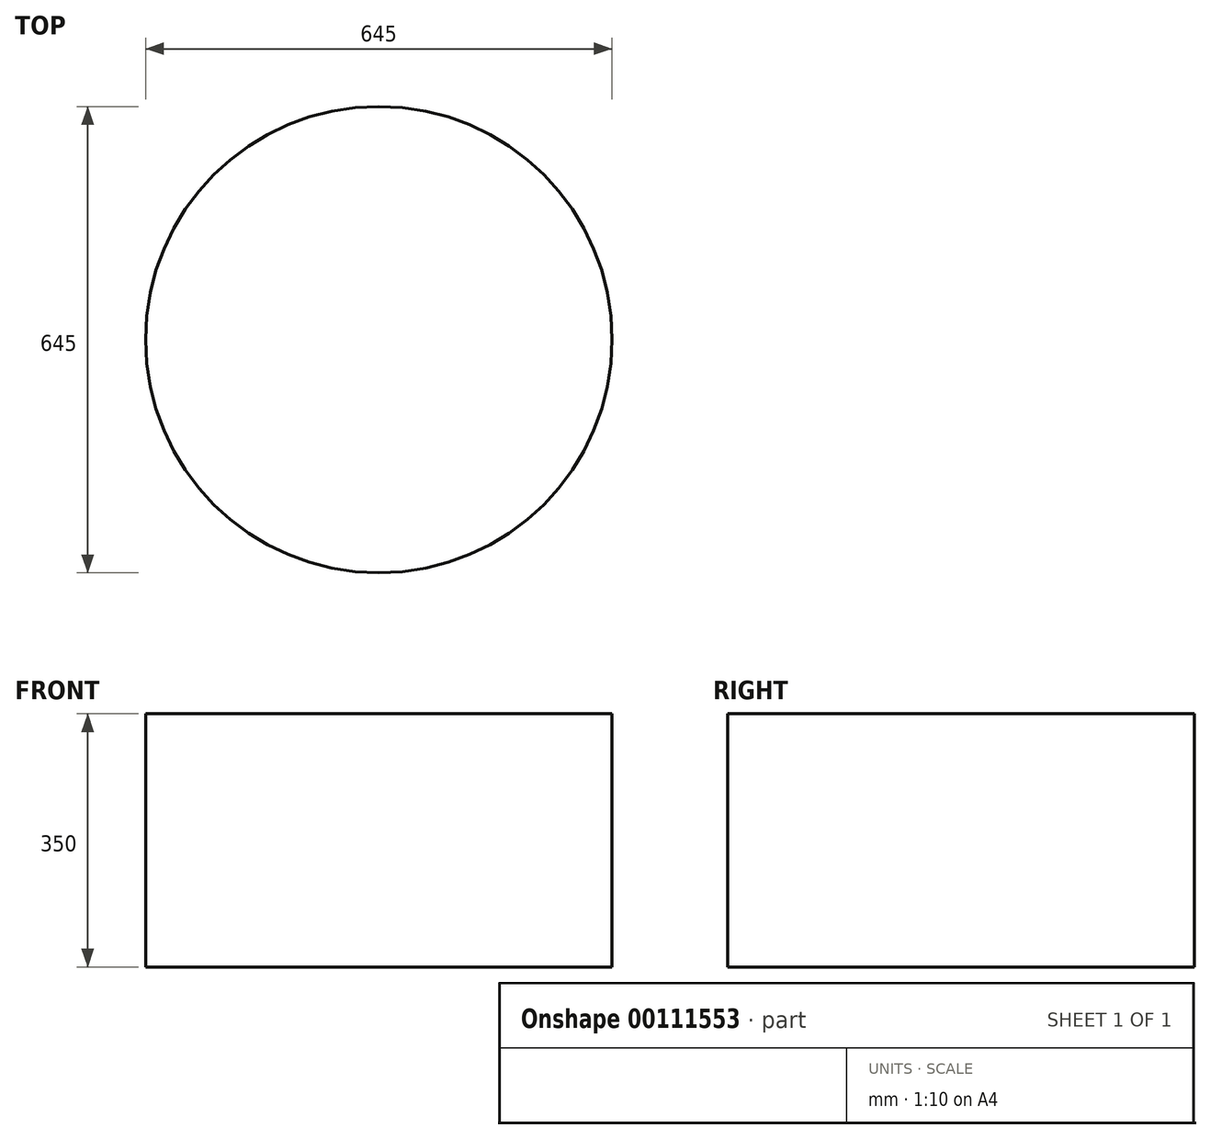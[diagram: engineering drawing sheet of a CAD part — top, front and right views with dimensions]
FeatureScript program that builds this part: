
annotation { "Feature Type Name" : "Feature", "Feature Type Description" : "" }
export const myFeature = defineFeature(function(context is Context, id is Id, definition is map)
    precondition{}
    {
        {
            var Q0;
            Q0=qCreatedBy(makeId("Top.planeOp"),FACE);
            var sketch = newSketch(context, id + "F0", { "sketchPlane" : qUnion([Q0])});
            skCircle(sketch, "E0", {"center": v(0, 0) * mm, "radius": 322.5 * mm});
            skSolve(sketch);
        }
        {
            var Q0;
            Q0 = qSketchRegion(id + "F0", true);
            extrude(context, id + "F1", {"entities" : qUnion([Q0]), "depth" : 350 * mm});
        }
    });
